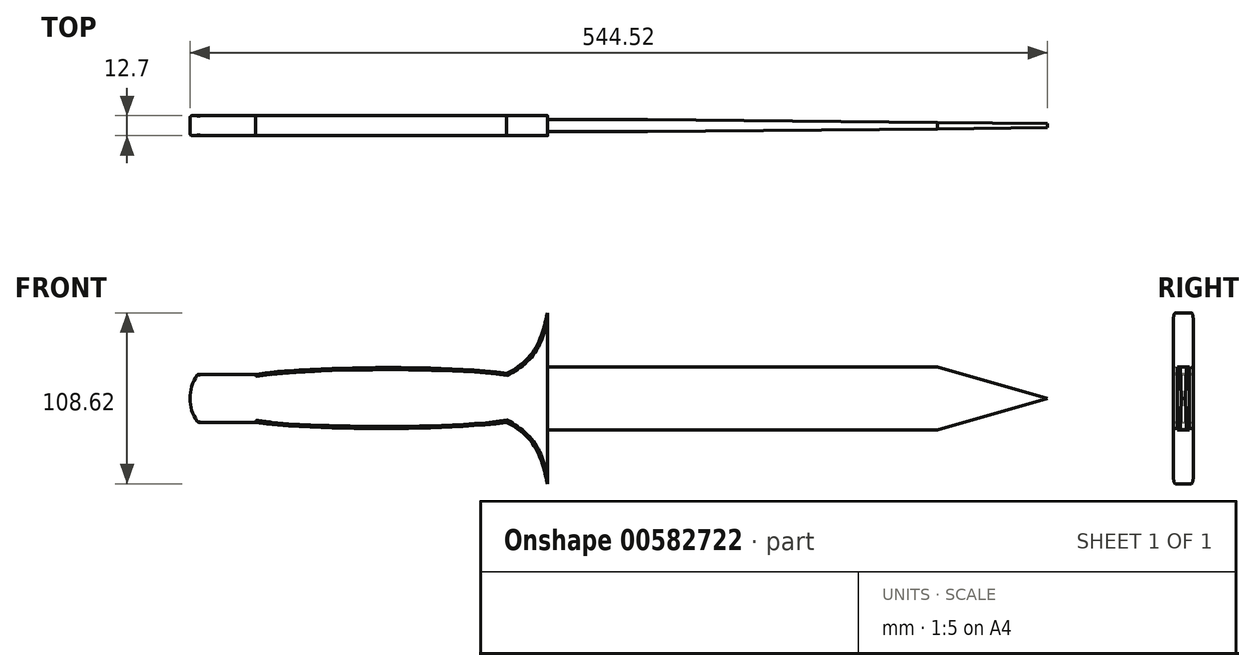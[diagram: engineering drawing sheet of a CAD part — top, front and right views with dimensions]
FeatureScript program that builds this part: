
annotation { "Feature Type Name" : "Feature", "Feature Type Description" : "" }
export const myFeature = defineFeature(function(context is Context, id is Id, definition is map)
    precondition{}
    {
        {
            var Q0;
            Q0=qCreatedBy(makeId("Front.planeOp"),FACE);
            var sketch = newSketch(context, id + "F0", { "sketchPlane" : qUnion([Q0])});
            skLineSegment(sketch, "E0", {"start": v(-74.36, 0) * mm, "end": v(-74.36, -15.24) * mm});
            skLineSegment(sketch, "E1", {"start": v(-74.36, 0) * mm, "end": v(-74.36, 15.24) * mm});
            skArc(sketch, "E2", {"start": v(-74.36, 15.24) * mm, "mid": v(-79.23, 0) * mm, "end": v(-74.36, -15.24) * mm});
            skLineSegment(sketch, "E3", {"start": v(-74.36, 15.24) * mm, "end": v(-37.53, 15.24) * mm});
            skLineSegment(sketch, "E4", {"start": v(-74.36, -15.24) * mm, "end": v(-37.53, -15.24) * mm});
            skFitSpline(sketch, "E5", {"points": [v(-37.53, -15.24) * mm, v(121.87, -15.24) * mm], "startDerivative": vector(94.44, -15.66) * mm, "endDerivative": vector(97.18, 15.65) * mm});
            skLineSegment(sketch, "E6", {"start": v(121.87, -15.24) * mm, "end": v(121.87, 15.69) * mm, "construction": true});
            skFitSpline(sketch, "E7", {"points": [v(-37.53, 15.24) * mm, v(121.87, 15.69) * mm], "startDerivative": vector(99.62, 15.93) * mm, "endDerivative": vector(99.3, -15.93) * mm});
            skFitSpline(sketch, "E8", {"points": [v(121.87, 15.69) * mm, v(147.8, 54.3) * mm], "startDerivative": vector(59.6, 30.73) * mm, "endDerivative": vector(10.85, 44.44) * mm});
            skLineSegment(sketch, "E9", {"start": v(121.87, 15.69) * mm, "end": v(150.96, 15.69) * mm, "construction": true});
            skLineSegment(sketch, "E10", {"start": v(121.87, -15.24) * mm, "end": v(150.95, -15.24) * mm, "construction": true});
            skFitSpline(sketch, "E11", {"points": [v(121.87, -15.24) * mm, v(147.8, -54.33) * mm], "startDerivative": vector(59.6, -30.7) * mm, "endDerivative": vector(10.85, -44.45) * mm});
            skLineSegment(sketch, "E12", {"start": v(147.8, 54.3) * mm, "end": v(147.8, -54.33) * mm});
            skPoint(sketch, "E13.endSnap0", {"position": v(136.41, 15.69) * mm});
            skLineSegment(sketch, "E14", {"start": v(147.8, -54.33) * mm, "end": v(147.8, -19.99) * mm, "construction": true});
            skLineSegment(sketch, "E15", {"start": v(147.8, 54.3) * mm, "end": v(147.8, 19.95) * mm, "construction": true});
            skLineSegment(sketch, "E16", {"start": v(147.8, 19.95) * mm, "end": v(395.44, 19.95) * mm});
            skLineSegment(sketch, "E17", {"start": v(147.8, -19.99) * mm, "end": v(395.44, -19.99) * mm});
            skLineSegment(sketch, "E18", {"start": v(147.8, 0) * mm, "end": v(465.3, 0) * mm, "construction": true});
            skLineSegment(sketch, "E19", {"start": v(395.44, 19.95) * mm, "end": v(465.3, 0) * mm});
            skLineSegment(sketch, "E20", {"start": v(465.3, 0) * mm, "end": v(395.44, -19.99) * mm});
            skLineSegment(sketch, "E21", {"start": v(147.8, 19.95) * mm, "end": v(147.8, -19.99) * mm});
            skSolve(sketch);
        }
        {
            var Q0;
            Q0=makeQuery(id+"F0.imprint","IMPRINT",FACE,{"disambiguationData":[TD([[makeQuery(id+"F0.imprint","IMPRINT",EDGE,{"derivedFrom":sQuery(id+"F0.wireOp",EDGE,"E0")}),1.0]])]});
            var Q1;
            Q1=makeQuery(id+"F0.imprint","IMPRINT",FACE,{"disambiguationData":[TD([[makeQuery(id+"F0.imprint","IMPRINT",EDGE,{"derivedFrom":sQuery(id+"F0.wireOp",EDGE,"E0")}),-1.0]])]});
            extrude(context, id + "F1", {"entities" : qUnion([Q0, Q1]), "depth" : 12.7 * mm, "offsetDistance" : 25.4 * mm, "symmetric" : true});
        }
        {
            var Q0;
            Q0=makeQuery(id+"F1.opExtrude","CAP_EDGE",EDGE,{"disambiguationData":[OSD([sQuery(id+"F0.wireOp",EDGE,"E7")])],"isStart":false});
            var Q1;
            Q1=makeQuery(id+"F1.opExtrude","CAP_EDGE",EDGE,{"disambiguationData":[OSD([sQuery(id+"F0.wireOp",EDGE,"E7")])],"isStart":true});
            var Q2;
            Q2=makeQuery(id+"F1.opExtrude","CAP_EDGE",EDGE,{"disambiguationData":[OSD([sQuery(id+"F0.wireOp",EDGE,"E5")])],"isStart":false});
            var Q3;
            Q3=makeQuery(id+"F1.opExtrude","CAP_EDGE",EDGE,{"disambiguationData":[OSD([sQuery(id+"F0.wireOp",EDGE,"E5")])],"isStart":true});
            var Q4;
            Q4=makeQuery(id+"F1.opExtrude","CAP_EDGE",EDGE,{"disambiguationData":[OSD([sQuery(id+"F0.wireOp",EDGE,"E3")])],"isStart":false});
            var Q5;
            Q5=makeQuery(id+"F1.opExtrude","CAP_EDGE",EDGE,{"disambiguationData":[OSD([sQuery(id+"F0.wireOp",EDGE,"E3")])],"isStart":true});
            var Q6;
            Q6=makeQuery(id+"F1.opExtrude","CAP_EDGE",EDGE,{"disambiguationData":[OSD([sQuery(id+"F0.wireOp",EDGE,"E4")])],"isStart":true});
            var Q7;
            Q7=makeQuery(id+"F1.opExtrude","CAP_EDGE",EDGE,{"disambiguationData":[OSD([sQuery(id+"F0.wireOp",EDGE,"E4")])],"isStart":false});
            var Q8;
            Q8=makeQuery(id+"F1.opExtrude","CAP_EDGE",EDGE,{"disambiguationData":[OSD([sQuery(id+"F0.wireOp",EDGE,"E11")])],"isStart":true});
            var Q9;
            Q9=makeQuery(id+"F1.opExtrude","CAP_EDGE",EDGE,{"disambiguationData":[OSD([sQuery(id+"F0.wireOp",EDGE,"E11")])],"isStart":false});
            var Q10;
            Q10=makeQuery(id+"F1.opExtrude","CAP_EDGE",EDGE,{"disambiguationData":[OSD([sQuery(id+"F0.wireOp",EDGE,"E8")])],"isStart":true});
            var Q11;
            Q11=makeQuery(id+"F1.opExtrude","CAP_EDGE",EDGE,{"disambiguationData":[OSD([sQuery(id+"F0.wireOp",EDGE,"E8")])],"isStart":false});
            fillet(context, id + "F2", {"entities" : qUnion([Q0, Q1, Q2, Q3, Q4, Q5, Q6, Q7, Q8, Q9, Q10, Q11]), "radius" : 1.27 * mm, "tangentPropagation" : true, "allowEdgeOverflow" : false});
        }
        {
            var Q0;
            Q0=makeQuery(id+"F1.opExtrude","SWEPT_EDGE",EDGE,{"disambiguationData":[OSD([sQuery(id+"F0.wireOp",EDGE,"E1"),sQuery(id+"F0.wireOp",EDGE,"E2"),sQuery(id+"F0.wireOp",EDGE,"E3")])]});
            var Q1;
            Q1=makeQuery(id+"F1.opExtrude","SWEPT_EDGE",EDGE,{"disambiguationData":[OSD([sQuery(id+"F0.wireOp",EDGE,"E0"),sQuery(id+"F0.wireOp",EDGE,"E2"),sQuery(id+"F0.wireOp",EDGE,"E4")])]});
            fillet(context, id + "F3", {"entities" : qUnion([Q0, Q1]), "radius" : 1.27 * mm, "tangentPropagation" : true, "allowEdgeOverflow" : false});
        }
        {
            var Q0;
            Q0=makeQuery(id+"F0.imprint","IMPRINT",FACE,{"disambiguationData":[TD([[makeQuery(id+"F0.imprint","IMPRINT",EDGE,{"derivedFrom":sQuery(id+"F0.wireOp",EDGE,"E16")}),-1.0]])]});
            extrude(context, id + "F4", {"entities" : qUnion([Q0]), "depth" : 7.62 * mm, "offsetDistance" : 25.4 * mm, "symmetric" : true});
        }
        {
            var Q0;
            Q0=makeQuery(id+"F4.opExtrude","SWEPT_FACE",FACE,{"disambiguationData":[OSD([sQuery(id+"F0.wireOp",EDGE,"E17")])]});
            var sketch = newSketch(context, id + "F5", { "sketchPlane" : qUnion([Q0])});
            skLineSegment(sketch, "E22.0", {"start": v(465.3, 3.81) * mm, "end": v(465.3, -3.81) * mm});
            skLineSegment(sketch, "E23.0", {"start": v(465.3, 3.81) * mm, "end": v(395.44, 3.81) * mm});
            skLineSegment(sketch, "E24.0", {"start": v(147.8, 3.81) * mm, "end": v(395.44, 3.81) * mm});
            skLineSegment(sketch, "E25", {"start": v(147.8, 3.81) * mm, "end": v(211.3, 3.81) * mm, "construction": true});
            skLineSegment(sketch, "E26", {"start": v(465.3, 3.81) * mm, "end": v(465.3, 1.27) * mm, "construction": true});
            skLineSegment(sketch, "E27", {"start": v(465.3, -3.81) * mm, "end": v(465.3, -1.27) * mm, "construction": true});
            skLineSegment(sketch, "E28", {"start": v(211.3, 3.81) * mm, "end": v(465.3, 1.27) * mm});
            skLineSegment(sketch, "E29", {"start": v(211.3, -3.8) * mm, "end": v(465.3, -1.27) * mm});
            skLineSegment(sketch, "E30", {"start": v(465.3, 1.27) * mm, "end": v(465.3, -1.27) * mm});
            skLineSegment(sketch, "E31.0", {"start": v(465.3, -3.81) * mm, "end": v(395.44, -3.81) * mm});
            skLineSegment(sketch, "E32.0", {"start": v(147.8, -3.81) * mm, "end": v(395.44, -3.81) * mm});
            skSolve(sketch);
        }
        {
            var Q0;
            {var subQ0=sQuery(id+"F5.wireOp",EDGE,"E24.0");var subQ3=sQuery(id+"F5.wireOp",EDGE,"E28");var subQ4=makeQuery(id+"F5.imprint","INTERSECT",VERTEX,{"derivedFrom":[subQ0,subQ3]});Q0=makeQuery(id+"F5.imprint","IMPRINT",FACE,{"disambiguationData":[TD([[makeQuery(id+"F5.imprint","IMPRINT",EDGE,{"disambiguationData":[TD([[subQ4,-1.0]])],"derivedFrom":subQ3}),1.0]])]});}
            var Q1;
            {var subQ0=sQuery(id+"F5.wireOp",EDGE,"E23.0");Q1=makeQuery(id+"F5.imprint","IMPRINT",FACE,{"disambiguationData":[TD([[makeQuery(id+"F5.imprint","IMPRINT",EDGE,{"derivedFrom":subQ0}),1.0]])]});}
            var Q2;
            {var subQ0=sQuery(id+"F5.wireOp",EDGE,"E31.0");Q2=makeQuery(id+"F5.imprint","IMPRINT",FACE,{"disambiguationData":[TD([[makeQuery(id+"F5.imprint","IMPRINT",EDGE,{"derivedFrom":subQ0}),-1.0]])]});}
            var Q3;
            {var subQ0=sQuery(id+"F5.wireOp",EDGE,"E32.0");var subQ1=sQuery(id+"F5.wireOp",EDGE,"E29");var subQ2=makeQuery(id+"F5.imprint","INTERSECT",VERTEX,{"derivedFrom":[subQ1,subQ0]});Q3=makeQuery(id+"F5.imprint","IMPRINT",FACE,{"disambiguationData":[TD([[makeQuery(id+"F5.imprint","IMPRINT",EDGE,{"disambiguationData":[TD([[subQ2,-1.0]])],"derivedFrom":subQ1}),-1.0]])]});}
            extrude(context, id + "F6", {"entities" : qUnion([Q0, Q1, Q2, Q3]), "operationType" : NewBodyOperationType.REMOVE, "oppositeDirection" : true, "depth" : 50.8 * mm, "offsetDistance" : 25.4 * mm});
        }
    });
